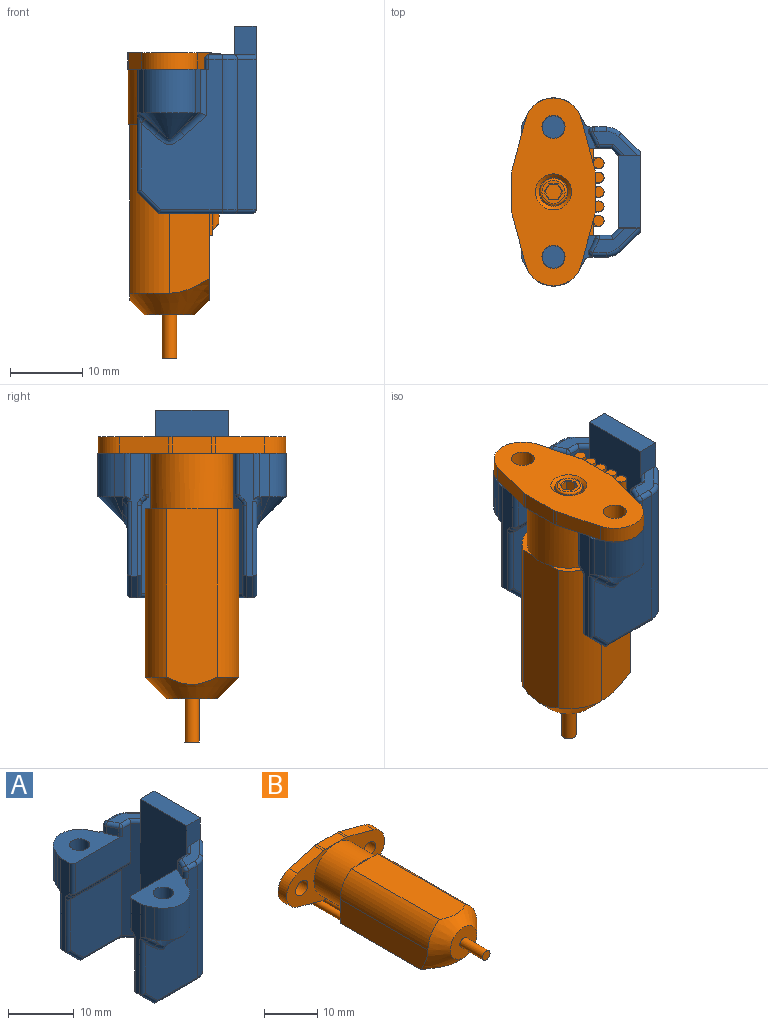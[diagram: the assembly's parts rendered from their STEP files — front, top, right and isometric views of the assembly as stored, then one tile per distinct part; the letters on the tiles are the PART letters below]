
ASSEMBLY  parts=2 mates=1
PART A: 110 faces, bbox 17.5x26.4x26.3 mm
  f0: plane 10.83x7.05mm, normal (0,0,1), area 48.2mm2, adj f3,f5,f9,f10,f11,f12,f13,f24
  f1: plane 20.88x2.08mm, normal (-0.71,0.71,0), area 47.7mm2, adj f2,f4,f12,f16,f23,f40,f41,f49
  f2: plane 12.15x10.9mm, normal (0,1,0), area 128.9mm2, adj f1,f43,f45,f47,f49
  f3: plane 20.8x11.19mm, normal (0,-1,0), area 135.9mm2, adj f0,f22,f27,f30,f33,f35,f37,f50
  f4: plane 25.4x10mm, normal (-1,0,0), area 254mm2, adj f1,f20,f21,f39,f59,f75
  f5: plane 17.33x2.27mm, normal (-1,0,0), area 20.8mm2, adj f0,f15,f33,f42,f46,f47,f48,f54
  f6: plane 20.8x2.59mm, normal (0.71,-0.71,0), area 76.1mm2, adj f7,f22,f32,f36
  f7: plane 25.57x11.24mm, normal (1,0,0), area 276.7mm2, adj f6,f20,f21,f32,f34,f63,f75,f86
  f8: plane 16.8x12.9mm, normal (0,0,-1), area 43.6mm2, adj f15,f34,f36,f37,f38,f39,f40,f43
  f9: cylinder r=4.05mm len=7.29mm, axis (0,0,1), area 54.4mm2, adj f0,f10,f11,f18
  f10: plane 6.02x1.21mm, normal (0.9,-0.44,0), area 8mm2, adj f0,f9,f19,f50,f51
  f11: plane 6x1.35mm, normal (-0.9,-0.44,0), area 9mm2, adj f0,f9,f17,f55
  f12: plane 11.9x7.15mm, normal (0,1,0), area 70.8mm2, adj f0,f1,f24,f25,f41,f42
  f13: plane 1.8x1.4mm, normal (-0.9,0.44,0), area 2.8mm2, adj f0,f24,f27,f28
  f14: plane 6.23x3.4mm, normal (0,0,1), area 8.7mm2, adj f20,f23,f25,f28,f30,f31,f32
  f15: plane 3x3mm, normal (-0.71,0,-0.71), area 3.4mm2, adj f5,f8,f35,f45
  f16: plane 11.72x0.65mm, normal (0,0.71,-0.71), area 10.5mm2, adj f1,f41,f46,f49
  f17: plane 2.95x2.47mm, normal (-0.64,-0.31,-0.71), area 2.2mm2, adj f11,f18,f53,f54,f55
  f18: cone r=4.05mm half-angle=45deg, axis (0,0,1), area 25.2mm2, adj f9,f17,f19,f52
  f19: plane 2.74x2.46mm, normal (0.64,-0.31,-0.71), area 2.1mm2, adj f10,f18,f51
  f20: plane 4.85x3.25mm, normal (0,-1,0), area 12.1mm2, adj f4,f7,f14,f21,f23,f32
  f21: plane 10x3mm, normal (0,0,1), area 30mm2, adj f4,f7,f20,f75
  f22: cylinder r=3mm len=20.8mm, axis (0,0,1), area 49mm2, adj f3,f6,f31,f38
  f23: cylinder r=0.6mm len=2.02mm, axis (-0.71,-0.71,0), area 1.7mm2, adj f1,f14,f20,f25
  f24: cylinder r=0.6mm len=1.4mm, axis (0,0,1), area 0.9mm2, adj f0,f12,f13,f26
  f25: cylinder r=0.6mm len=1.92mm, axis (-1,0,0), area 1.7mm2, adj f12,f14,f23,f26
  f26: sphere r=0.6mm, area 0.4mm2, adj f24,f25,f28
  f27: cylinder r=0.6mm len=1.4mm, axis (0,0,-1), area 1.7mm2, adj f0,f3,f13,f29
  f28: cylinder r=0.6mm len=2.06mm, axis (0.44,0.9,0), area 1.9mm2, adj f13,f14,f26,f29
  f29: sphere r=0.6mm, area 0.7mm2, adj f27,f28,f30
  f30: cylinder r=0.6mm len=1.84mm, axis (1,0,0), area 1.7mm2, adj f3,f14,f29,f31
  f31: torus R=2.4mm, axis (0,0,1), area 2.1mm2, adj f14,f22,f30,f32
  f32: cylinder r=0.6mm len=3.28mm, axis (0.71,0.71,0), area 3.6mm2, adj f6,f7,f14,f20,f31
  f33: cylinder r=0.6mm len=10.39mm, axis (0,0,1), area 9.4mm2, adj f3,f5,f35,f54
  f34: cylinder r=0.6mm len=11.07mm, axis (0,-1,0), area 10.2mm2, adj f7,f8,f36,f89
  f35: cylinder r=0.6mm len=3.42mm, axis (0.71,0,-0.71), area 3.8mm2, adj f3,f15,f33,f37
  f36: cylinder r=0.6mm len=3.01mm, axis (-0.71,-0.71,0), area 3.3mm2, adj f6,f8,f34,f38
  f37: cylinder r=0.6mm len=8.79mm, axis (-1,0,0), area 8.2mm2, adj f3,f8,f35,f38
  f38: torus R=2.4mm, axis (0,0,1), area 2.1mm2, adj f8,f22,f36,f37
  f39: cylinder r=0.6mm len=10.5mm, axis (0,1,0), area 9.7mm2, adj f4,f8,f40,f92
  f40: cylinder r=0.6mm len=2.78mm, axis (0.71,0.71,0), area 2.9mm2, adj f1,f8,f39,f43
  f41: cylinder r=0.6mm len=11.9mm, axis (-1,0,0), area 5.6mm2, adj f1,f12,f16,f44
  f42: cylinder r=0.6mm len=5.75mm, axis (0,0,-1), area 5.4mm2, adj f0,f5,f12,f44
  f43: cylinder r=0.6mm len=8.75mm, axis (1,0,0), area 8mm2, adj f2,f8,f40,f45
  f44: sphere r=0.6mm, area 0.2mm2, adj f41,f42,f46
  f45: cylinder r=0.6mm len=3.42mm, axis (-0.71,0,0.71), area 3.8mm2, adj f2,f15,f43,f47
  f46: cylinder r=0.6mm len=1.07mm, axis (0,0.71,0.71), area 0.9mm2, adj f5,f16,f44,f48
  f47: cylinder r=0.6mm len=9.75mm, axis (0,0,1), area 9.1mm2, adj f2,f5,f45,f48
  f48: torus R=1.2mm, axis (-1,0,0), area 0.6mm2, adj f5,f46,f47,f49
  f49: cylinder r=0.6mm len=11.08mm, axis (1,0,0), area 5.2mm2, adj f1,f2,f16,f48
  f50: cylinder r=1mm len=6.41mm, axis (0,0,1), area 7mm2, adj f0,f3,f10,f51
  f51: cylinder r=1mm len=3.7mm, axis (-0.74,0,-0.67), area 4.9mm2, adj f3,f10,f19,f50,f52
  f52: bspline ~5.24x2.61mm, area 4.6mm2, adj f3,f18,f51,f53
  f53: cylinder r=1mm len=2.47mm, axis (0.74,0,-0.67), area 3.1mm2, adj f3,f17,f52,f54
  f54: bspline ~1.61x1.6mm, area 1.3mm2, adj f5,f17,f33,f53,f55
  f55: cylinder r=2mm len=6.47mm, axis (0,0,1), area 5.5mm2, adj f0,f5,f11,f17,f54
  f56: cylinder r=1.55mm len=7mm, axis (0,0,1), area 68.2mm2, adj f0,f57
  f57: plane 3.1x3.1mm, normal (0,0,1), area 7.5mm2, adj f56
  f58: plane 10.83x7.05mm, normal (0,0,1), area 48.2mm2, adj f61,f62,f64,f65,f66,f67,f68,f78
  f59: plane 20.88x2.08mm, normal (-0.71,-0.71,0), area 47.7mm2, adj f4,f60,f67,f71,f77,f92,f93,f101
  f60: plane 12.15x10.9mm, normal (0,-1,0), area 128.9mm2, adj f59,f95,f97,f99,f101
  f61: plane 20.8x11.19mm, normal (0,1,0), area 135.9mm2, adj f58,f76,f81,f84,f87,f88,f90,f102
  f62: plane 17.33x2.27mm, normal (-1,0,0), area 20.8mm2, adj f58,f70,f87,f94,f98,f99,f100,f106
  f63: plane 20.8x2.59mm, normal (0.71,0.71,0), area 76.1mm2, adj f7,f76,f86,f89
  f64: cylinder r=4.05mm len=7.29mm, axis (0,0,1), area 54.4mm2, adj f58,f65,f66,f73
  f65: plane 6.02x1.21mm, normal (0.9,0.44,0), area 8mm2, adj f58,f64,f74,f102,f103
  f66: plane 6x1.35mm, normal (-0.9,0.44,0), area 9mm2, adj f58,f64,f72,f107
  f67: plane 11.9x7.15mm, normal (0,-1,0), area 70.8mm2, adj f58,f59,f78,f79,f93,f94
  f68: plane 1.8x1.4mm, normal (-0.9,-0.44,0), area 2.8mm2, adj f58,f78,f81,f82
  f69: plane 6.23x3.4mm, normal (0,0,1), area 8.7mm2, adj f75,f77,f79,f82,f84,f85,f86
  f70: plane 3x3mm, normal (-0.71,0,-0.71), area 3.4mm2, adj f8,f62,f88,f97
  f71: plane 11.72x0.65mm, normal (0,-0.71,-0.71), area 10.5mm2, adj f59,f93,f98,f101
  f72: plane 2.95x2.47mm, normal (-0.64,0.31,-0.71), area 2.2mm2, adj f66,f73,f105,f106,f107
  f73: cone r=4.05mm half-angle=45deg, axis (0,0,1), area 25.2mm2, adj f64,f72,f74,f104
  f74: plane 2.74x2.46mm, normal (0.64,0.31,-0.71), area 2.1mm2, adj f65,f73,f103
  f75: plane 4.85x3.25mm, normal (0,1,0), area 12.1mm2, adj f4,f7,f21,f69,f77,f86
  f76: cylinder r=3mm len=20.8mm, axis (0,0,1), area 49mm2, adj f61,f63,f85,f91
  f77: cylinder r=0.6mm len=2.02mm, axis (-0.71,0.71,0), area 1.7mm2, adj f59,f69,f75,f79
  f78: cylinder r=0.6mm len=1.4mm, axis (0,0,1), area 0.9mm2, adj f58,f67,f68,f80
  f79: cylinder r=0.6mm len=1.92mm, axis (-1,0,0), area 1.7mm2, adj f67,f69,f77,f80
  f80: sphere r=0.6mm, area 0.4mm2, adj f78,f79,f82
  f81: cylinder r=0.6mm len=1.4mm, axis (0,0,-1), area 1.7mm2, adj f58,f61,f68,f83
  f82: cylinder r=0.6mm len=2.06mm, axis (0.44,-0.9,0), area 1.9mm2, adj f68,f69,f80,f83
  f83: sphere r=0.6mm, area 0.9mm2, adj f81,f82,f84
  f84: cylinder r=0.6mm len=1.84mm, axis (1,0,0), area 1.7mm2, adj f61,f69,f83,f85
  f85: torus R=2.4mm, axis (0,0,1), area 2.1mm2, adj f69,f76,f84,f86
  f86: cylinder r=0.6mm len=3.28mm, axis (0.71,-0.71,0), area 3.6mm2, adj f7,f63,f69,f75,f85
  f87: cylinder r=0.6mm len=10.39mm, axis (0,0,1), area 9.4mm2, adj f61,f62,f88,f106
  f88: cylinder r=0.6mm len=3.42mm, axis (0.71,0,-0.71), area 3.8mm2, adj f61,f70,f87,f90
  f89: cylinder r=0.6mm len=3.01mm, axis (-0.71,0.71,0), area 3.3mm2, adj f8,f34,f63,f91
  f90: cylinder r=0.6mm len=8.79mm, axis (-1,0,0), area 8.2mm2, adj f8,f61,f88,f91
  f91: torus R=2.4mm, axis (0,0,1), area 2.1mm2, adj f8,f76,f89,f90
  f92: cylinder r=0.6mm len=2.78mm, axis (0.71,-0.71,0), area 2.9mm2, adj f8,f39,f59,f95
  f93: cylinder r=0.6mm len=11.9mm, axis (-1,0,0), area 5.6mm2, adj f59,f67,f71,f96
  f94: cylinder r=0.6mm len=5.75mm, axis (0,0,-1), area 5.4mm2, adj f58,f62,f67,f96
  f95: cylinder r=0.6mm len=8.75mm, axis (1,0,0), area 8mm2, adj f8,f60,f92,f97
  f96: sphere r=0.6mm, area 0.2mm2, adj f93,f94,f98
  f97: cylinder r=0.6mm len=3.42mm, axis (-0.71,0,0.71), area 3.8mm2, adj f60,f70,f95,f99
  f98: cylinder r=0.6mm len=1.07mm, axis (0,-0.71,0.71), area 0.9mm2, adj f62,f71,f96,f100
  f99: cylinder r=0.6mm len=9.75mm, axis (0,0,1), area 9.1mm2, adj f60,f62,f97,f100
  f100: torus R=1.2mm, axis (-1,0,0), area 0.6mm2, adj f62,f98,f99,f101
  f101: cylinder r=0.6mm len=11.08mm, axis (1,0,0), area 5.2mm2, adj f59,f60,f71,f100
  f102: cylinder r=1mm len=6.41mm, axis (0,0,1), area 7mm2, adj f58,f61,f65,f103
  f103: cylinder r=1mm len=3.7mm, axis (-0.74,0,-0.67), area 4.9mm2, adj f61,f65,f74,f102,f104
  f104: bspline ~5.24x2.61mm, area 4.6mm2, adj f61,f73,f103,f105
  f105: cylinder r=1mm len=2.47mm, axis (0.74,0,-0.67), area 3.1mm2, adj f61,f72,f104,f106
  f106: bspline ~1.61x1.6mm, area 1.3mm2, adj f62,f72,f87,f105,f107
  f107: cylinder r=2mm len=6.47mm, axis (0,0,1), area 5.5mm2, adj f58,f62,f66,f72,f106
  f108: cylinder r=1.55mm len=7mm, axis (0,0,1), area 68.2mm2, adj f58,f109
  f109: plane 3.1x3.1mm, normal (0,0,1), area 7.5mm2, adj f108
PART B: 106 faces, bbox 27.6x43.9x18.6 mm
  f0: plane 2.31x2mm, normal (0,1,0), area 3.5mm2, adj f1,f2,f3,f4,f5,f6
  f1: plane 1.9x1.15mm, normal (-1,0,0), area 2.2mm2, adj f0,f2,f6,f7
  f2: plane 1.9x1mm, normal (-0.5,0,0.87), area 2.2mm2, adj f0,f1,f3,f8
  f3: plane 1.9x1mm, normal (0.5,0,0.87), area 2.2mm2, adj f0,f2,f4,f9
  f4: plane 1.9x1.15mm, normal (1,0,0), area 2.2mm2, adj f0,f3,f5,f10
  f5: plane 1.9x1mm, normal (0.5,0,-0.87), area 2.2mm2, adj f0,f4,f6,f11
  f6: plane 1.9x1mm, normal (-0.5,0,-0.87), area 2.2mm2, adj f0,f1,f5,f12
  f7: plane 1.27x0.1mm, normal (-0.71,0.71,0), area 0.2mm2, adj f1,f8,f12,f13
  f8: plane 1.1x0.69mm, normal (-0.35,0.71,0.61), area 0.2mm2, adj f2,f7,f9,f13
  f9: plane 1.1x0.69mm, normal (0.35,0.71,0.61), area 0.2mm2, adj f3,f8,f10,f13
  f10: plane 1.27x0.1mm, normal (0.71,0.71,0), area 0.2mm2, adj f4,f9,f11,f13
  f11: plane 1.1x0.69mm, normal (0.35,0.71,-0.61), area 0.2mm2, adj f5,f10,f12,f13
  f12: plane 1.1x0.69mm, normal (-0.35,0.71,-0.61), area 0.2mm2, adj f6,f7,f11,f13
  f13: plane 3.2x3.2mm, normal (0,1,0), area 3.9mm2, adj f7,f8,f9,f10,f11,f12,f14
  f14: torus R=1.6mm, axis (0,1,0), area 5.3mm2, adj f13,f15
  f15: cylinder r=1.9mm len=9.7mm, axis (0,1,0), area 115.8mm2, adj f14,f16
  f16: plane 4x4mm, normal (0,1,0), area 1.2mm2, adj f15,f17
  f17: cylinder r=2mm len=9.5mm, axis (0,-1,0), area 119.4mm2, adj f16,f18
  f18: cone r=2.25mm half-angle=45deg, axis (0,1,0), area 10mm2, adj f17,f23
  f19: plane 0.36x0.03mm, normal (0,-1,0), area 0mm2, adj f37,f38
  f20: plane 0.36x0.03mm, normal (0,-1,0), area 0mm2, adj f40,f41
  f21: plane 0.36x0.03mm, normal (0,-1,0), area 0mm2, adj f44,f45
  f22: plane 0.36x0.03mm, normal (0,-1,0), area 0mm2, adj f48,f49
  f23: plane 26x11.53mm, normal (0,1,0), area 202.8mm2, adj f18,f25,f26,f27,f28,f29,f30,f31
  f24: plane 0.36x0.03mm, normal (0,-1,0), area 0mm2, adj f52,f53
  f25: cylinder r=2mm len=2.3mm, axis (0,-1,0), area 1.2mm2, adj f23,f42,f46,f54
  f26: cylinder r=4mm len=7.72mm, axis (0,-1,0), area 24mm2, adj f23,f27,f46,f54
  f27: plane 6.79x2.3mm, normal (0.26,0,0.97), area 16.2mm2, adj f23,f26,f28,f54
  f28: cylinder r=2mm len=2.3mm, axis (0,-1,0), area 1.2mm2, adj f23,f27,f29,f54
  f29: plane 5.47x2.3mm, normal (0,0,1), area 12.6mm2, adj f23,f28,f30,f54
  f30: cylinder r=2mm len=2.3mm, axis (0,-1,0), area 1.2mm2, adj f23,f29,f31,f54
  f31: plane 6.79x2.3mm, normal (-0.26,0,0.97), area 16.2mm2, adj f23,f30,f32,f54
  f32: cylinder r=4mm len=7.72mm, axis (0,-1,0), area 24mm2, adj f23,f31,f50,f54
  f33: cylinder r=2mm len=2.3mm, axis (0,-1,0), area 1.2mm2, adj f23,f42,f50,f54
  f34: cylinder r=1.6mm len=3.2mm, axis (0,-1,0), area 23.1mm2, adj f23,f54
  f35: cylinder r=1.6mm len=3.2mm, axis (0,-1,0), area 23.1mm2, adj f23,f54
  f36: plane 1.5x1.24mm, normal (0,1,0), area 1.6mm2, adj f42,f55
  f37: plane 1.11x0.88mm, normal (0,-0.71,-0.71), area 0.9mm2, adj f19,f38,f56
  f38: cone r=0.75mm half-angle=5deg, axis (0,1,0), area 7mm2, adj f19,f37,f55,f56
  f39: plane 1.5x1.24mm, normal (0,1,0), area 1.6mm2, adj f42,f57
  f40: plane 1.11x0.88mm, normal (0,-0.71,-0.71), area 0.9mm2, adj f20,f41,f58
  f41: cone r=0.75mm half-angle=5deg, axis (0,1,0), area 7.1mm2, adj f20,f40,f57,f58
  f42: plane 5.47x2.3mm, normal (0,0,-1), area 4.9mm2, adj f23,f25,f33,f36,f39,f43,f54,f55
  f43: plane 1.5x1.24mm, normal (0,1,0), area 1.6mm2, adj f42,f59
  f44: plane 1.11x0.88mm, normal (0,-0.71,-0.71), area 0.9mm2, adj f21,f45,f60
  f45: cone r=0.75mm half-angle=5deg, axis (0,1,0), area 7.1mm2, adj f21,f44,f59,f60
  f46: plane 6.79x2.3mm, normal (0.26,0,-0.97), area 15.4mm2, adj f23,f25,f26,f47,f54,f61
  f47: plane 1.5x1.5mm, normal (0,1,0), area 1.8mm2, adj f46,f61
  f48: plane 1.11x0.88mm, normal (0,-0.71,-0.71), area 0.9mm2, adj f22,f49,f62
  f49: cone r=0.75mm half-angle=5deg, axis (0,1,0), area 7.1mm2, adj f22,f48,f61,f62
  f50: plane 6.79x2.3mm, normal (-0.26,0,-0.97), area 15.4mm2, adj f23,f32,f33,f51,f54,f63
  f51: plane 1.5x1.5mm, normal (0,1,0), area 1.8mm2, adj f50,f63
  f52: plane 1.31x0.9mm, normal (0,-0.71,-0.71), area 0.9mm2, adj f24,f53,f64
  f53: cone r=0.75mm half-angle=5deg, axis (0,1,0), area 7.1mm2, adj f24,f52,f63,f64
  f54: plane 26x11.53mm, normal (0,-1,0), area 118.1mm2, adj f25,f26,f27,f28,f29,f30,f31,f32
  f55: cylinder r=0.75mm len=21.25mm, axis (0,1,0), area 97.2mm2, adj f36,f38,f42,f54,f67,f68
  f56: plane 4.26x1.76mm, normal (0,0,-1), area 2.4mm2, adj f37,f38,f66,f67,f68,f69,f70
  f57: cylinder r=0.75mm len=21.25mm, axis (0,1,0), area 88mm2, adj f39,f41,f42,f54,f65,f71,f72,f73
  f58: plane 4.04x1.54mm, normal (0,0,-1), area 2.4mm2, adj f40,f41,f73,f74,f75,f76,f77
  f59: cylinder r=0.75mm len=21.25mm, axis (0,1,0), area 97.2mm2, adj f42,f43,f45,f54,f78,f82
  f60: plane 4.04x1.54mm, normal (0,0,-1), area 2.4mm2, adj f44,f45,f78,f79,f80,f81,f82
  f61: cylinder r=0.75mm len=21.25mm, axis (0,1,0), area 99.3mm2, adj f46,f47,f49,f54,f83,f87
  f62: plane 4.04x1.54mm, normal (0,0,-1), area 2.4mm2, adj f48,f49,f83,f84,f85,f86,f87
  f63: cylinder r=0.75mm len=21.25mm, axis (0,1,0), area 99.3mm2, adj f50,f51,f53,f54,f88,f92
  f64: plane 4.04x1.54mm, normal (0,0,-1), area 2.4mm2, adj f52,f53,f88,f89,f90,f91,f92
  f65: cylinder r=5.75mm len=11.5mm, axis (0,-1,0), area 269.9mm2, adj f54,f57,f71,f72,f93,f94,f95,f97
  f66: plane 4x0.51mm, normal (1,0,0), area 2mm2, adj f56,f67,f70,f97
  f67: plane 0.75x0.51mm, normal (0,1,0), area 0.1mm2, adj f55,f56,f66,f97
  f68: plane 0.75x0.51mm, normal (0,1,0), area 0.1mm2, adj f55,f56,f69,f97
  f69: plane 4x0.51mm, normal (-1,0,0), area 2mm2, adj f56,f68,f70,f97
  f70: plane 1.5x0.51mm, normal (0,-1,0), area 0.8mm2, adj f56,f66,f69,f97
  f71: plane 1.68x0.24mm, normal (0,-1,0), area 0.2mm2, adj f57,f65,f97
  f72: plane 1.68x0.24mm, normal (0,-1,0), area 0.2mm2, adj f57,f65,f97
  f73: plane 0.75x0.51mm, normal (0,1,0), area 0.1mm2, adj f57,f58,f74,f97
  f74: plane 4x0.51mm, normal (-1,0,0), area 2mm2, adj f58,f73,f75,f97
  f75: plane 1.5x0.51mm, normal (0,-1,0), area 0.8mm2, adj f58,f74,f76,f97
  f76: plane 4x0.51mm, normal (1,0,0), area 2mm2, adj f58,f75,f77,f97
  f77: plane 0.75x0.51mm, normal (0,1,0), area 0.1mm2, adj f57,f58,f76,f97
  f78: plane 0.75x0.51mm, normal (0,1,0), area 0.1mm2, adj f59,f60,f79,f97
  f79: plane 4x0.51mm, normal (-1,0,0), area 2mm2, adj f60,f78,f80,f97
  f80: plane 1.5x0.51mm, normal (0,-1,0), area 0.8mm2, adj f60,f79,f81,f97
  f81: plane 4x0.51mm, normal (1,0,0), area 2mm2, adj f60,f80,f82,f97
  f82: plane 0.75x0.51mm, normal (0,1,0), area 0.1mm2, adj f59,f60,f81,f97
  f83: plane 0.75x0.51mm, normal (0,1,0), area 0.1mm2, adj f61,f62,f84,f97
  f84: plane 4x0.51mm, normal (-1,0,0), area 2mm2, adj f62,f83,f85,f97
  f85: plane 1.5x0.51mm, normal (0,-1,0), area 0.8mm2, adj f62,f84,f86,f97
  f86: plane 4x0.51mm, normal (1,0,0), area 2mm2, adj f62,f85,f87,f97
  f87: plane 0.75x0.51mm, normal (0,1,0), area 0.1mm2, adj f61,f62,f86,f97
  f88: plane 0.75x0.51mm, normal (0,1,0), area 0.1mm2, adj f63,f64,f89,f97
  f89: plane 4x0.51mm, normal (-1,0,0), area 2mm2, adj f64,f88,f90,f97
  f90: plane 1.5x0.51mm, normal (0,-1,0), area 0.8mm2, adj f64,f89,f91,f97
  f91: plane 4x0.51mm, normal (1,0,0), area 2mm2, adj f64,f90,f92,f97
  f92: plane 0.75x0.51mm, normal (0,1,0), area 0.1mm2, adj f63,f64,f91,f97
  f93: plane 10.99x4.82mm, normal (0,1,0), area 15.2mm2, adj f65,f97,f98,f99,f100
  f94: plane 3.35x0.25mm, normal (0,-1,0), area 0.6mm2, adj f65,f100
  f95: plane 10.99x4.82mm, normal (0,1,0), area 15.2mm2, adj f65,f96,f97,f100,f101
  f96: plane 24.9x7.08mm, normal (-1,0,0), area 124.1mm2, adj f95,f97,f101,f102
  f97: plane 24.34x13.03mm, normal (0,0,-1), area 272mm2, adj f65,f66,f67,f68,f69,f70,f71,f72
  f98: plane 24x6.19mm, normal (1,0,0), area 124.1mm2, adj f93,f97,f99,f102
  f99: cylinder r=6.5mm len=23.31mm, axis (0,-1,0), area 152.9mm2, adj f93,f98,f100,f102
  f100: plane 24.75x6.93mm, normal (0,0,1), area 166.1mm2, adj f93,f94,f95,f99,f101,f102
  f101: cylinder r=6.5mm len=23.31mm, axis (0,-1,0), area 152.9mm2, adj f95,f96,f100,f102
  f102: cone r=8.51mm half-angle=45deg, axis (0,1,0), area 137.1mm2, adj f96,f97,f98,f99,f100,f101,f103
  f103: plane 7.03x7.03mm, normal (0,-1,0), area 35.7mm2, adj f102,f105
  f104: plane 2x2mm, normal (0,-1,0), area 3.1mm2, adj f105
  f105: cylinder r=1mm len=6mm, axis (0,-1,0), area 37.7mm2, adj f103,f104
PLACE A t=(2.47,-21.27,7.43)mm fixed
PLACE B rot(axis=(0.58,-0.58,-0.58),120deg) t=(2.47,-21.27,9.73)mm
MATE fastened B.f26 <-> A.f56  axis (0,0,-1) through (2.47,-30.27,7.43)mm
